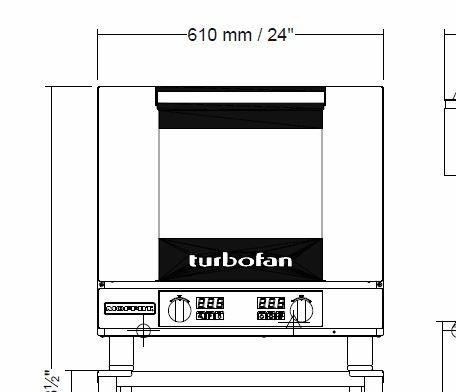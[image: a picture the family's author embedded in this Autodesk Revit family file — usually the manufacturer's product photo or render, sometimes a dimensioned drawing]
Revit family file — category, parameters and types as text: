
# Revit family: QF_MOFFAT_E30M3-2C_UK
name_source: partatom
category: Specialty Equipment
revit_build: Autodesk Revit 2014 (Build: 20130308_1515(x64)
units: mm (PartAtom-declared; Revit-internal decimal feet)

## types (1)
- QF_MOFFAT_E30M3-2C_UK
    Apparent Power = 2185 VA
    Conn Conduit = Yes
    Depth = 666 mm  [stored 2.18504 ft]
    Description = GN 1/1 MANUAL / ELECTRIC CONVECTION OVENS DOUBLE STACKED ON A STAINLESS STEEL BASE STAND
    Elec Conn Connection Height = 0 mm  [stored 0 ft]
    Elec Conn RI Height = 0 mm  [stored 0 ft]
    Electrical Remarks = 230-240V, 50Hz, 1P+N+E, 2.3kW, 9.5A
    Exhaust RI Height = 0 mm  [stored 0 ft]
    Exhaust Static Press = 0.00 in-wg
    Exhaust Vent Depth = 0 mm  [stored 0 ft]
    Exhaust Vent Diameter = 0 mm  [stored 0 ft]
    Exhaust Vent Width = 0 mm  [stored 0 ft]
    Exhaust Volume = 0 CFM
    FL Amps = 10 A
    Foodservice Equipment Identifier = Yes
    Height = 1718 mm  [stored 5.63648 ft]
    Height of Stand = 536 mm  [stored 1.75853 ft]
    Identify Quantity as Lot = Yes
    Length = 810 mm
    Manufacturer = MOFFAT
    Max Overcurrent Protection = 0 A
    Min Ckt Ampacity = 0 A
    Model = E30M3-2C
    Number of Poles = 1
    Phase = 1
    Volts = 230 V
    Watts = 2300 W
    Weight in Pounds = 0

note: [stored X ft] marks values corroborated as IEEE doubles in the binary element streams (Revit-internal decimal feet)

## geometry (parser evidence)
native form markers: Blend x14, Sweep x7
no freeform markers — native parametric forms only
